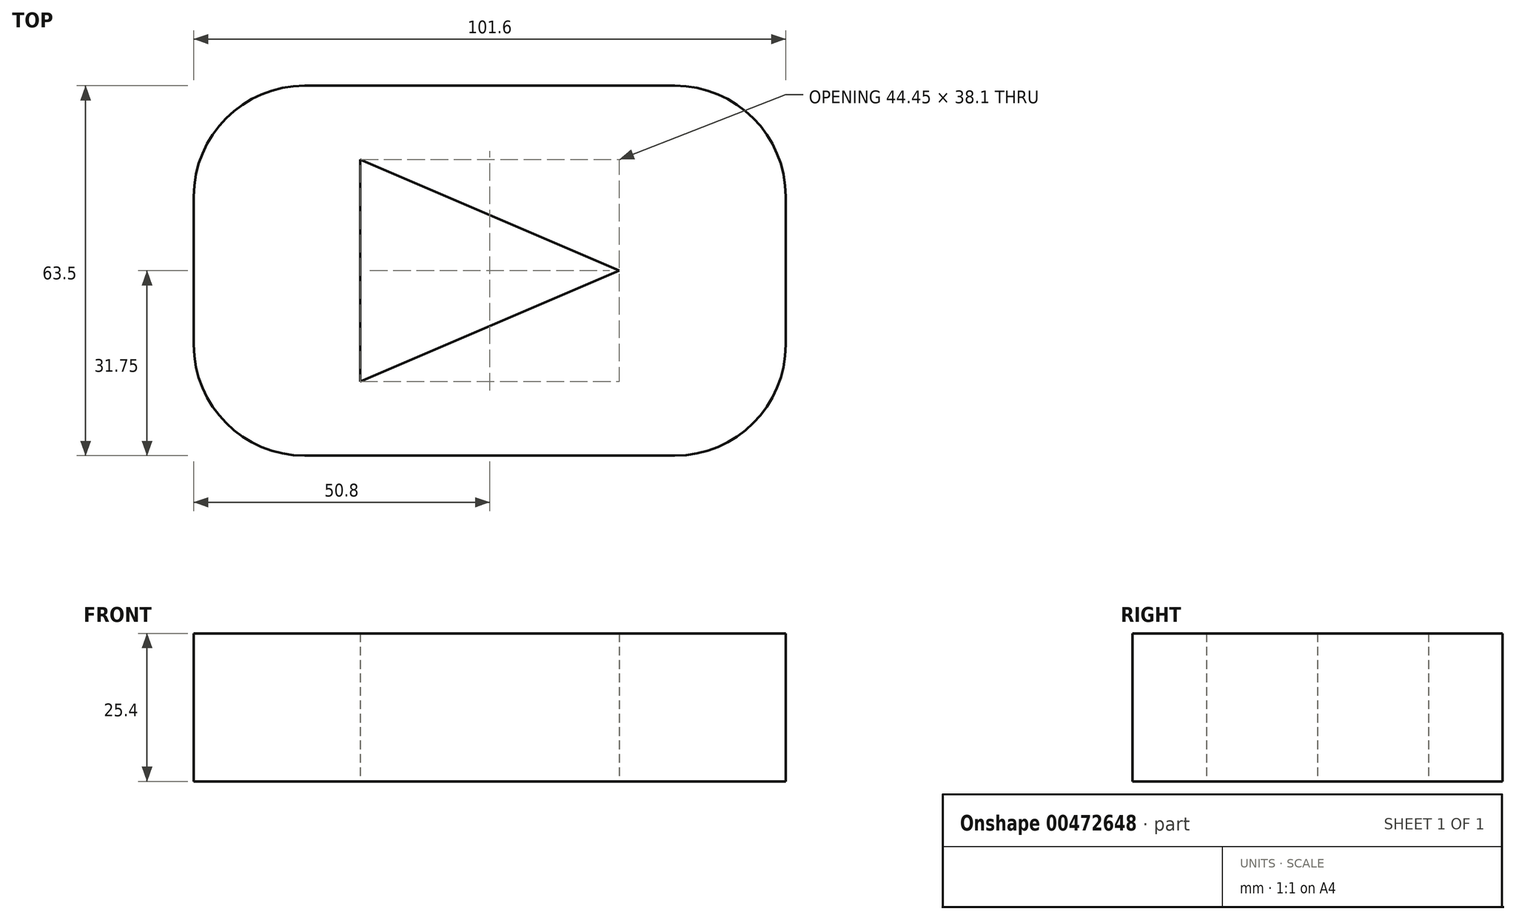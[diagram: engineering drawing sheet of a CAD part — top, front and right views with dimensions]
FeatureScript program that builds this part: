
annotation { "Feature Type Name" : "Feature", "Feature Type Description" : "" }
export const myFeature = defineFeature(function(context is Context, id is Id, definition is map)
    precondition{}
    {
        {
            var Q0;
            Q0=qCreatedBy(makeId("Top.planeOp"),FACE);
            var sketch = newSketch(context, id + "F0", { "sketchPlane" : qUnion([Q0])});
            skLineSegment(sketch, "E0.bottom", {"start": v(31.75, 31.75) * mm, "end": v(-31.75, 31.75) * mm});
            skLineSegment(sketch, "E0.top", {"start": v(31.75, -31.75) * mm, "end": v(-31.75, -31.75) * mm});
            skLineSegment(sketch, "E0.left", {"start": v(50.8, 12.7) * mm, "end": v(50.8, -12.7) * mm});
            skLineSegment(sketch, "E0.right", {"start": v(-50.8, 12.7) * mm, "end": v(-50.8, -12.7) * mm});
            skPoint(sketch, "E0.middle", {"position": v(0, 0) * mm});
            skPoint(sketch, "E1.visualSharp", {"position": v(-50.8, 31.75) * mm});
            skArc(sketch, "E1.filletArc", {"start": v(-31.75, 31.75) * mm, "mid": v(-45.22, 26.17) * mm, "end": v(-50.8, 12.7) * mm});
            skPoint(sketch, "E2.visualSharp", {"position": v(50.8, 31.75) * mm});
            skArc(sketch, "E2.filletArc", {"start": v(50.8, 12.7) * mm, "mid": v(45.22, 26.17) * mm, "end": v(31.75, 31.75) * mm});
            skPoint(sketch, "E3.visualSharp", {"position": v(50.8, -31.75) * mm});
            skArc(sketch, "E3.filletArc", {"start": v(31.75, -31.75) * mm, "mid": v(45.22, -26.17) * mm, "end": v(50.8, -12.7) * mm});
            skPoint(sketch, "E4.visualSharp", {"position": v(-50.8, -31.75) * mm});
            skArc(sketch, "E4.filletArc", {"start": v(-50.8, -12.7) * mm, "mid": v(-45.22, -26.17) * mm, "end": v(-31.75, -31.75) * mm});
            skLineSegment(sketch, "E5", {"start": v(22.23, 0) * mm, "end": v(-22.23, 19.05) * mm});
            skLineSegment(sketch, "E6", {"start": v(-22.23, 19.05) * mm, "end": v(-22.22, -19.05) * mm});
            skLineSegment(sketch, "E7", {"start": v(-22.23, -19.05) * mm, "end": v(22.23, 0) * mm});
            skSolve(sketch);
        }
        {
            var Q0;
            Q0=makeQuery(id+"F0.imprint","IMPRINT",FACE,{"disambiguationData":[TD([[makeQuery(id+"F0.imprint","IMPRINT",EDGE,{"derivedFrom":sQuery(id+"F0.wireOp",EDGE,"E0.bottom")}),1.0]])]});
            extrude(context, id + "F1", {"entities" : qUnion([Q0]), "depth" : 25.4 * mm});
        }
    });
